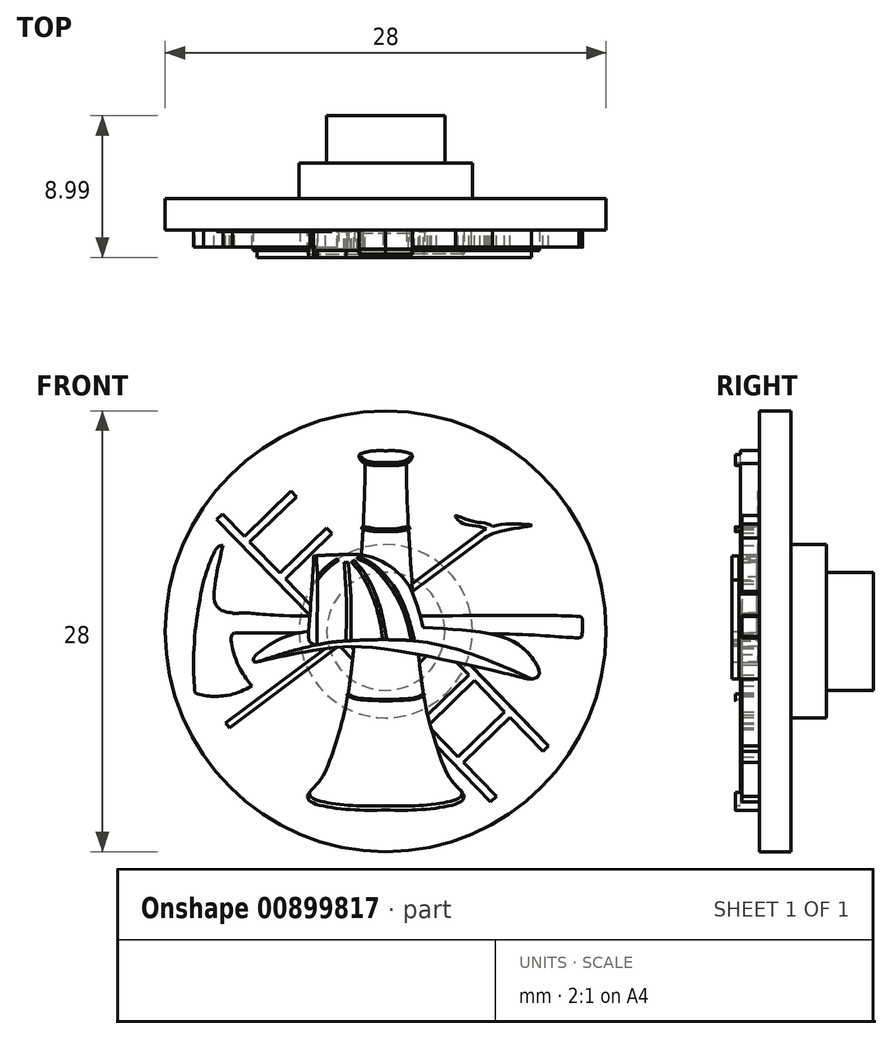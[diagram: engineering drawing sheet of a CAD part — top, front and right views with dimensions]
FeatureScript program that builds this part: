
annotation { "Feature Type Name" : "Feature", "Feature Type Description" : "" }
export const myFeature = defineFeature(function(context is Context, id is Id, definition is map)
    precondition{}
    {
        {
            var Q0;
            Q0=qCreatedBy(makeId("Top.planeOp"),FACE);
            var sketch = newSketch(context, id + "F0", { "sketchPlane" : qUnion([Q0])});
            skLineSegment(sketch, "E0", {"start": v(0, 0) * mm, "end": v(-14, 0) * mm});
            skLineSegment(sketch, "E1", {"start": v(-14, 0) * mm, "end": v(-14, 2) * mm});
            skLineSegment(sketch, "E2", {"start": v(-14, 2) * mm, "end": v(-5.5, 2) * mm});
            skLineSegment(sketch, "E3", {"start": v(-5.5, 2) * mm, "end": v(-5.5, 4.25) * mm});
            skLineSegment(sketch, "E4", {"start": v(-5.5, 4.25) * mm, "end": v(-3.75, 4.25) * mm});
            skLineSegment(sketch, "E5", {"start": v(-3.75, 4.25) * mm, "end": v(-3.75, 7.25) * mm});
            skLineSegment(sketch, "E6", {"start": v(-3.75, 7.25) * mm, "end": v(0, 7.25) * mm});
            skLineSegment(sketch, "E7", {"start": v(0, 7.25) * mm, "end": v(0, 0) * mm});
            skSolve(sketch);
        }
        {
            var Q0;
            Q0=makeQuery(id+"F0.imprint","IMPRINT",FACE,{"disambiguationData":[TD([[makeQuery(id+"F0.imprint","IMPRINT",EDGE,{"derivedFrom":sQuery(id+"F0.wireOp",EDGE,"E0")}),-1.0]])]});
            var Q1;
            Q1=sQuery(id+"F0.wireOp",EDGE,"E7");
            revolve(context, id + "F1", {"surfaceOperationType" : NewSurfaceOperationType.NEW, "entities" : qUnion([Q0]), "axis" : qUnion([Q1]), "revolveType" : RevolveType.FULL});
        }
        {
            var Q0;
            Q0=makeQuery(id+"F1.opRevolve","SWEPT_FACE",FACE,{"disambiguationData":[OSD([sQuery(id+"F0.wireOp",EDGE,"E0")])]});
            var sketch = newSketch(context, id + "F2", { "sketchPlane" : qUnion([Q0])});
            skFitSpline(sketch, "E8", {"points": [v(-4.9, 0) * mm, v(-6.87, -0.58) * mm, v(-8.37, -1.68) * mm, v(-8.37, -1.91) * mm, v(-8.17, -1.94) * mm, v(-7.37, -1.76) * mm, v(-4.83, -1.26) * mm, v(-0.5, -1.08) * mm, v(8.76, -2.96) * mm, v(9.26, -3.03) * mm, v(9.64, -2.89) * mm, v(9.74, -2.52) * mm, v(8.83, -1.16) * mm, v(7, -0.24) * mm, v(2.37, 0.26) * mm], "startDerivative": vector(-35.31, -5.38) * mm, "endDerivative": vector(-43.26, 2.75) * mm});
            skFitSpline(sketch, "E9", {"points": [v(-8.17, -1.94) * mm, v(-5.98, -1.26) * mm, v(-3.2, -0.69) * mm, v(0.5, -0.54) * mm, v(2.72, -0.73) * mm, v(5.57, -1.5) * mm, v(9.26, -3.03) * mm], "startDerivative": vector(14.7, 4.83) * mm, "endDerivative": vector(19.38, -8.65) * mm});
            skFitSpline(sketch, "E10", {"points": [v(2.37, 0.26) * mm, v(1.88, 1.97) * mm, v(1, 3.5) * mm, v(-0.83, 4.69) * mm, v(-2.82, 4.87) * mm, v(-4.57, 4.77) * mm, v(-4.58, 4.74) * mm, v(-4.9, 0) * mm], "startDerivative": vector(-2.96, 11.42) * mm, "endDerivative": vector(-2.12, -28.99) * mm});
            skFitSpline(sketch, "E11", {"points": [v(-4.9, 0) * mm, v(-4.9, -0.32) * mm, v(-4.9, -0.47) * mm, v(-4.84, -0.63) * mm, v(-4.71, -0.76) * mm, v(-4.56, -0.84) * mm, v(-4.38, -0.87) * mm], "startDerivative": vector(-0.09, -1.67) * mm, "endDerivative": vector(1.14, -0.23) * mm});
            skFitSpline(sketch, "E12", {"points": [v(-4.42, 4.8) * mm, v(-4.3, 2.68) * mm, v(-4.38, -0.87) * mm], "startDerivative": vector(0.36, -4.54) * mm, "endDerivative": vector(-0.25, -6.7) * mm});
            skFitSpline(sketch, "E13", {"points": [v(-3.3, 4.85) * mm, v(-2.95, 4.47) * mm, v(-2.16, 4.43) * mm, v(-1.61, 4.85) * mm], "startDerivative": vector(0.93, -1.49) * mm, "endDerivative": vector(1.38, 1.52) * mm});
            skFitSpline(sketch, "E14", {"points": [v(-3.1, 4.58) * mm, v(-3.57, 4.26) * mm, v(-4.33, 3.45) * mm], "startDerivative": vector(-1.19, -0.58) * mm, "endDerivative": vector(-1.01, -1.73) * mm});
            skFitSpline(sketch, "E15", {"points": [v(-4.32, 3.25) * mm, v(-3.5, 4.14) * mm, v(-3, 4.5) * mm], "startDerivative": vector(1.26, 1.99) * mm, "endDerivative": vector(1.19, 0.64) * mm});
            skFitSpline(sketch, "E16", {"points": [v(-2.65, 4.38) * mm, v(-2.5, 2.04) * mm, v(-2.52, -0.62) * mm], "startDerivative": vector(0.38, -4.75) * mm, "endDerivative": vector(-0.12, -5.26) * mm});
            skFitSpline(sketch, "E17", {"points": [v(-2.37, 4.38) * mm, v(-2.2, 2.04) * mm, v(-2.22, -0.6) * mm], "startDerivative": vector(0.43, -4.74) * mm, "endDerivative": vector(-0.12, -5.23) * mm});
            skFitSpline(sketch, "E18", {"points": [v(-2.18, 4.42) * mm, v(-1.46, 3.46) * mm, v(-0.77, 2.02) * mm, v(-0.43, 0.87) * mm, v(-0.19, -0.53) * mm], "startDerivative": vector(3.15, -3.72) * mm, "endDerivative": vector(0.9, -5.7) * mm});
            skFitSpline(sketch, "E19", {"points": [v(-2, 4.5) * mm, v(-1.28, 3.62) * mm, v(-0.56, 2.13) * mm, v(-0.21, 0.93) * mm, v(0.06, -0.53) * mm], "startDerivative": vector(3.23, -3.46) * mm, "endDerivative": vector(1, -5.88) * mm});
            skFitSpline(sketch, "E20", {"points": [v(-1.83, 4.63) * mm, v(-0.84, 4.1) * mm, v(0.22, 2.9) * mm, v(1.07, 1.4) * mm, v(1.62, -0.59) * mm], "startDerivative": vector(4.78, -2.05) * mm, "endDerivative": vector(1.66, -7.34) * mm});
            skFitSpline(sketch, "E21", {"points": [v(-1.73, 4.73) * mm, v(-0.8, 4.28) * mm, v(0.38, 3.04) * mm, v(1.23, 1.48) * mm, v(1.83, -0.6) * mm], "startDerivative": vector(4.6, -1.74) * mm, "endDerivative": vector(1.86, -7.6) * mm});
            skSolve(sketch);
        }
        {
            var Q0;
            Q0=makeQuery(id+"F1.opRevolve","SWEPT_FACE",FACE,{"disambiguationData":[OSD([sQuery(id+"F0.wireOp",EDGE,"E0")])]});
            var sketch = newSketch(context, id + "F3", { "sketchPlane" : qUnion([Q0])});
            skFitSpline(sketch, "E22", {"points": [v(-1.3, 10.65) * mm, v(-1.42, 6.93) * mm, v(-2.3, -3.39) * mm, v(-2.96, -6.4) * mm, v(-3.66, -8.52) * mm, v(-4.31, -9.64) * mm, v(-4.96, -10.4) * mm, v(-4.84, -10.76) * mm, v(-3.9, -11.11) * mm, v(-1.9, -11.35) * mm, v(0, -11.35) * mm], "startDerivative": vector(-0.32, -23.25) * mm, "endDerivative": vector(20.07, 0.5) * mm});
            skFitSpline(sketch, "E23", {"points": [v(-2.4, -3.98) * mm, v(-1.81, -4.23) * mm, v(-1.11, -4.3) * mm, v(-0.55, -4.33) * mm, v(0, -4.33) * mm], "startDerivative": vector(2.26, -1.15) * mm, "endDerivative": vector(2.35, 0.04) * mm});
            skFitSpline(sketch, "E24", {"points": [v(-2.4, -3.98) * mm, v(-2.45, -4) * mm, v(-2.41, -4.08) * mm, v(-1.83, -4.31) * mm, v(-1.1, -4.38) * mm, v(-0.55, -4.4) * mm, v(0, -4.41) * mm], "startDerivative": vector(-1, -0.29) * mm, "endDerivative": vector(2.72, -0.01) * mm});
            skFitSpline(sketch, "E25", {"points": [v(-4.86, -10.22) * mm, v(-4.72, -10.55) * mm, v(-3.84, -10.86) * mm, v(-1.97, -11.07) * mm, v(0, -11.1) * mm], "startDerivative": vector(0.49, -2.53) * mm, "endDerivative": vector(6.03, 0) * mm});
            skFitSpline(sketch, "E26", {"points": [v(0, 6.5) * mm, v(-0.7, 6.52) * mm, v(-1.44, 6.63) * mm, v(-1.52, 6.58) * mm, v(-1.51, 6.52) * mm, v(-0.74, 6.35) * mm, v(0, 6.34) * mm], "startDerivative": vector(-3.13, -0.1) * mm, "endDerivative": vector(3.11, 0.12) * mm});
            skFitSpline(sketch, "E27", {"points": [v(0, 11.46) * mm, v(-0.68, 11.46) * mm, v(-1.26, 11.38) * mm, v(-1.66, 11.21) * mm, v(-1.66, 10.98) * mm, v(-1.3, 10.65) * mm, v(0, 10.54) * mm], "startDerivative": vector(-3.85, 0.1) * mm, "endDerivative": vector(5.99, 0.16) * mm});
            skFitSpline(sketch, "E28", {"points": [v(0, 10.73) * mm, v(-1.23, 10.83) * mm, v(-1.66, 11.21) * mm], "startDerivative": vector(-2.37, -0.06) * mm, "endDerivative": vector(-0.85, 1.1) * mm});
            skFitSpline(sketch, "E29.MirrorCS", {"points": [v(0, 11.46) * mm, v(0.68, 11.46) * mm, v(1.26, 11.38) * mm, v(1.66, 11.21) * mm, v(1.66, 10.98) * mm, v(1.3, 10.65) * mm, v(0, 10.54) * mm], "startDerivative": vector(3.85, 0.1) * mm, "endDerivative": vector(-5.99, 0.16) * mm});
            skFitSpline(sketch, "E30.MirrorCS", {"points": [v(0, 10.73) * mm, v(1.23, 10.83) * mm, v(1.66, 11.21) * mm], "startDerivative": vector(2.37, -0.06) * mm, "endDerivative": vector(0.85, 1.1) * mm});
            skFitSpline(sketch, "E31.MirrorCS", {"points": [v(1.3, 10.65) * mm, v(1.42, 6.93) * mm, v(2.3, -3.39) * mm, v(2.96, -6.4) * mm, v(3.66, -8.52) * mm, v(4.31, -9.64) * mm, v(4.96, -10.4) * mm, v(4.84, -10.76) * mm, v(3.9, -11.11) * mm, v(1.9, -11.35) * mm, v(0, -11.35) * mm], "startDerivative": vector(0.32, -23.25) * mm, "endDerivative": vector(-20.07, 0.5) * mm});
            skFitSpline(sketch, "E32.MirrorCS", {"points": [v(0, 6.5) * mm, v(0.7, 6.52) * mm, v(1.44, 6.63) * mm, v(1.52, 6.58) * mm, v(1.51, 6.52) * mm, v(0.74, 6.35) * mm, v(0, 6.34) * mm], "startDerivative": vector(3.13, -0.1) * mm, "endDerivative": vector(-3.11, 0.12) * mm});
            skFitSpline(sketch, "E33.MirrorCS", {"points": [v(4.86, -10.22) * mm, v(4.72, -10.55) * mm, v(3.84, -10.86) * mm, v(1.97, -11.07) * mm, v(0, -11.1) * mm], "startDerivative": vector(-0.49, -2.53) * mm, "endDerivative": vector(-6.03, 0) * mm});
            skFitSpline(sketch, "E34.MirrorCS", {"points": [v(2.4, -3.98) * mm, v(1.81, -4.23) * mm, v(1.11, -4.3) * mm, v(0.55, -4.33) * mm, v(0, -4.33) * mm], "startDerivative": vector(-2.26, -1.15) * mm, "endDerivative": vector(-2.35, 0.04) * mm});
            skFitSpline(sketch, "E35.MirrorCS", {"points": [v(2.4, -3.98) * mm, v(2.45, -4) * mm, v(2.41, -4.08) * mm, v(1.83, -4.31) * mm, v(1.1, -4.38) * mm, v(0.55, -4.4) * mm, v(0, -4.41) * mm], "startDerivative": vector(1, -0.29) * mm, "endDerivative": vector(-2.72, -0.01) * mm});
            skSolve(sketch);
        }
        {
            var Q0;
            Q0=makeQuery(id+"F2.imprint","IMPRINT",FACE,{"disambiguationData":[TD([[makeQuery(id+"F2.imprint","IMPRINT",EDGE,{"derivedFrom":makeQuery(id+"F1.opRevolve","SWEPT_EDGE",EDGE,{"disambiguationData":[OSD([sQuery(id+"F0.wireOp",EDGE,"E0"),sQuery(id+"F0.wireOp",EDGE,"E1")])]})}),-1.0]])]});
            var sketch = newSketch(context, id + "F4", { "sketchPlane" : qUnion([Q0])});
            skLineSegment(sketch, "E36", {"start": v(7.02, -10.5) * mm, "end": v(-10.37, 7.46) * mm});
            skLineSegment(sketch, "E37", {"start": v(-10.37, 7.46) * mm, "end": v(-10.73, 7.11) * mm});
            skLineSegment(sketch, "E38", {"start": v(-10.73, 7.11) * mm, "end": v(6.66, -10.84) * mm});
            skLineSegment(sketch, "E39", {"start": v(6.66, -10.84) * mm, "end": v(7.02, -10.5) * mm});
            skLineSegment(sketch, "E40", {"start": v(-10.73, 7.11) * mm, "end": v(-6.65, 11.07) * mm, "construction": true});
            skLineSegment(sketch, "E41", {"start": v(6.66, -10.84) * mm, "end": v(10.92, -6.71) * mm, "construction": true});
            skLineSegment(sketch, "E42", {"start": v(-7.41, 10.33) * mm, "end": v(9.99, -7.62) * mm});
            skLineSegment(sketch, "E43", {"start": v(9.99, -7.62) * mm, "end": v(10.35, -7.27) * mm});
            skLineSegment(sketch, "E44", {"start": v(10.35, -7.27) * mm, "end": v(-7.05, 10.68) * mm});
            skLineSegment(sketch, "E45", {"start": v(-8.98, 6.02) * mm, "end": v(-6.02, 8.9) * mm});
            skLineSegment(sketch, "E46", {"start": v(-6.02, 8.9) * mm, "end": v(-5.67, 8.54) * mm});
            skLineSegment(sketch, "E47", {"start": v(-5.67, 8.54) * mm, "end": v(-8.63, 5.67) * mm});
            skLineSegment(sketch, "E48", {"start": v(-6.72, 3.7) * mm, "end": v(-3.76, 6.56) * mm});
            skLineSegment(sketch, "E49", {"start": v(-3.4, 6.2) * mm, "end": v(-6.37, 3.33) * mm});
            skLineSegment(sketch, "E50", {"start": v(-4.46, 1.36) * mm, "end": v(-1.5, 4.23) * mm});
            skLineSegment(sketch, "E51", {"start": v(-1.15, 3.87) * mm, "end": v(-4.11, 1) * mm});
            skLineSegment(sketch, "E52", {"start": v(-2.2, -0.98) * mm, "end": v(0.77, 1.9) * mm});
            skLineSegment(sketch, "E53", {"start": v(1.11, 1.53) * mm, "end": v(-1.85, -1.34) * mm});
            skLineSegment(sketch, "E54", {"start": v(3.03, -0.44) * mm, "end": v(0.06, -3.31) * mm});
            skLineSegment(sketch, "E55", {"start": v(0.41, -3.67) * mm, "end": v(3.38, -0.8) * mm});
            skLineSegment(sketch, "E56", {"start": v(5.29, -2.77) * mm, "end": v(2.33, -5.65) * mm});
            skLineSegment(sketch, "E57", {"start": v(2.33, -5.65) * mm, "end": v(2.67, -6) * mm});
            skLineSegment(sketch, "E58", {"start": v(2.67, -6) * mm, "end": v(5.64, -3.13) * mm});
            skLineSegment(sketch, "E59", {"start": v(7.55, -5.1) * mm, "end": v(4.59, -7.98) * mm});
            skLineSegment(sketch, "E60", {"start": v(4.59, -7.98) * mm, "end": v(4.94, -8.34) * mm});
            skLineSegment(sketch, "E61", {"start": v(4.94, -8.34) * mm, "end": v(7.9, -5.47) * mm});
            skLineSegment(sketch, "E62", {"start": v(-7.41, 10.33) * mm, "end": v(-7.05, 10.68) * mm});
            skSolve(sketch);
        }
        {
            var Q0;
            Q0=makeQuery(id+"F2.imprint","IMPRINT",FACE,{"disambiguationData":[TD([[makeQuery(id+"F2.imprint","IMPRINT",EDGE,{"derivedFrom":makeQuery(id+"F1.opRevolve","SWEPT_EDGE",EDGE,{"disambiguationData":[OSD([sQuery(id+"F0.wireOp",EDGE,"E0"),sQuery(id+"F0.wireOp",EDGE,"E1")])]})}),-1.0]])]});
            var sketch = newSketch(context, id + "F5", { "sketchPlane" : qUnion([Q0])});
            skLineSegment(sketch, "E63", {"start": v(-10.17, -5.8) * mm, "end": v(6, 6.23) * mm});
            skLineSegment(sketch, "E64", {"start": v(-10.17, -5.8) * mm, "end": v(-9.93, -6.13) * mm});
            skLineSegment(sketch, "E65", {"start": v(-9.93, -6.13) * mm, "end": v(6.28, 5.94) * mm});
            skFitSpline(sketch, "E66", {"points": [v(6, 6.23) * mm, v(7.48, 6.8) * mm, v(9.26, 6.72) * mm, v(7.7, 6.45) * mm, v(6.28, 5.94) * mm], "startDerivative": vector(3.7, 3.49) * mm, "endDerivative": vector(-4.19, -2.44) * mm});
            skFitSpline(sketch, "E67", {"points": [v(6.78, 6.66) * mm, v(6.3, 6.87) * mm, v(5.36, 7.03) * mm, v(4.42, 7.34) * mm, v(4.7, 6.96) * mm, v(5.29, 6.75) * mm, v(6.08, 6.62) * mm, v(6.38, 6.5) * mm], "startDerivative": vector(-2.93, 2.6) * mm, "endDerivative": vector(2.44, -1.25) * mm});
            skSolve(sketch);
        }
        {
            var Q0;
            Q0=makeQuery(id+"F2.imprint","IMPRINT",FACE,{"disambiguationData":[TD([[makeQuery(id+"F2.imprint","IMPRINT",EDGE,{"derivedFrom":makeQuery(id+"F1.opRevolve","SWEPT_EDGE",EDGE,{"disambiguationData":[OSD([sQuery(id+"F0.wireOp",EDGE,"E0"),sQuery(id+"F0.wireOp",EDGE,"E1")])]})}),-1.0]])]});
            var sketch = newSketch(context, id + "F6", { "sketchPlane" : qUnion([Q0])});
            skFitSpline(sketch, "E68", {"points": [v(-11.56, 3.2) * mm, v(-12, 0.78) * mm, v(-12.2, -2.34) * mm, v(-12.1, -3.93) * mm], "startDerivative": vector(-1.44, -6.68) * mm, "endDerivative": vector(0.51, -5.2) * mm});
            skFitSpline(sketch, "E69", {"points": [v(-12.1, -3.93) * mm, v(-11.33, -4.11) * mm, v(-10.57, -4.13) * mm, v(-9.66, -3.98) * mm, v(-8.5, -3.48) * mm], "startDerivative": vector(3.35, -0.94) * mm, "endDerivative": vector(4.06, 1.98) * mm});
            skFitSpline(sketch, "E70", {"points": [v(-8.5, -3.48) * mm, v(-9.36, -2.17) * mm, v(-9.8, -0.28) * mm, v(-9.59, -0.12) * mm], "startDerivative": vector(-2.28, 2.73) * mm, "endDerivative": vector(1.56, 0.49) * mm});
            skFitSpline(sketch, "E71", {"points": [v(-9.59, -0.12) * mm, v(-9.7, 0) * mm, v(-9.72, 1.16) * mm], "startDerivative": vector(-0.42, 0.28) * mm, "endDerivative": vector(0.09, 2) * mm});
            skFitSpline(sketch, "E72", {"points": [v(-9.72, 1.16) * mm, v(-10.32, 1.3) * mm, v(-10.78, 1.66) * mm, v(-10.88, 2.7) * mm, v(-10.34, 5.46) * mm], "startDerivative": vector(-3.36, 0.47) * mm, "endDerivative": vector(1.77, 7.66) * mm});
            skFitSpline(sketch, "E73", {"points": [v(-10.34, 5.46) * mm, v(-10.7, 5.31) * mm, v(-11.56, 3.2) * mm], "startDerivative": vector(-1.2, -0.16) * mm, "endDerivative": vector(-1.24, -3.83) * mm});
            skFitSpline(sketch, "E74", {"points": [v(-9.72, 1.11) * mm, v(-8.95, 1.16) * mm, v(-6.69, 1) * mm, v(8.74, 1.02) * mm, v(12.28, 0.94) * mm], "startDerivative": vector(7, 0.73) * mm, "endDerivative": vector(11.01, -0.48) * mm});
            skFitSpline(sketch, "E75", {"points": [v(12.28, 0.94) * mm, v(12.44, 0.88) * mm, v(12.46, -0.34) * mm], "startDerivative": vector(0.67, -0.04) * mm, "endDerivative": vector(-0.18, -2.2) * mm});
            skFitSpline(sketch, "E76", {"points": [v(12.46, -0.34) * mm, v(12.36, -0.4) * mm, v(9.57, -0.26) * mm, v(-9.59, -0.12) * mm], "startDerivative": vector(-1.31, -1.2) * mm, "endDerivative": vector(-33.19, -0.18) * mm});
            skSolve(sketch);
        }
        {
            var Q0;
            Q0=makeQuery(id+"F6.imprint","IMPRINT",FACE,{"disambiguationData":[TD([[makeQuery(id+"F6.imprint","IMPRINT",EDGE,{"derivedFrom":sQuery(id+"F6.wireOp",EDGE,"E68")}),1.0]])]});
            var Q1;
            {var subQ0=sQuery(id+"F6.wireOp",EDGE,"E74");var subQ1=sQuery(id+"F6.wireOp",EDGE,"E71");var subQ2=makeQuery(id+"F6.imprint","INTERSECT",VERTEX,{"derivedFrom":[subQ1,subQ0]});Q1=makeQuery(id+"F6.imprint","IMPRINT",FACE,{"disambiguationData":[TD([[makeQuery(id+"F6.imprint","IMPRINT",EDGE,{"disambiguationData":[TD([[subQ2,1.0]])],"derivedFrom":subQ1}),-1.0]])]});}
            var Q2;
            {var subQ1=sQuery(id+"F6.wireOp",EDGE,"E75");Q2=makeQuery(id+"F6.imprint","IMPRINT",FACE,{"disambiguationData":[TD([[makeQuery(id+"F6.imprint","IMPRINT",EDGE,{"derivedFrom":subQ1}),-1.0]])]});}
            extrude(context, id + "F7", {"entities" : qUnion([Q0, Q1, Q2]), "operationType" : NewBodyOperationType.ADD, "depth" : .1 * mm, "offsetDistance" : 25 * mm});
        }
        {
            var Q0;
            {var subQ0=sQuery(id+"F5.wireOp",EDGE,"E64");Q0=makeQuery(id+"F5.imprint","IMPRINT",FACE,{"disambiguationData":[TD([[makeQuery(id+"F5.imprint","IMPRINT",EDGE,{"derivedFrom":subQ0}),1.0]])]});}
            var Q1;
            {var subQ1=sQuery(id+"F5.wireOp",EDGE,"E66");var subQ9=sQuery(id+"F5.wireOp",EDGE,"E63");var subQ10=makeQuery(id+"F5.imprint","INTERSECT",VERTEX,{"derivedFrom":[subQ9,subQ1]});Q1=makeQuery(id+"F5.imprint","IMPRINT",FACE,{"disambiguationData":[TD([[makeQuery(id+"F5.imprint","IMPRINT",EDGE,{"disambiguationData":[TD([[subQ10,-1.0]])],"derivedFrom":subQ1}),-1.0]])]});}
            var Q2;
            {var subQ0=sQuery(id+"F5.wireOp",EDGE,"E67");Q2=makeQuery(id+"F5.imprint","IMPRINT",FACE,{"disambiguationData":[TD([[makeQuery(id+"F5.imprint","IMPRINT",EDGE,{"derivedFrom":subQ0}),1.0]])]});}
            extrude(context, id + "F8", {"entities" : qUnion([Q0, Q1, Q2]), "operationType" : NewBodyOperationType.ADD, "depth" : .1 * mm, "offsetDistance" : 25 * mm});
        }
        {
            var Q0;
            {var subQ10=sQuery(id+"F4.wireOp",EDGE,"E37");Q0=makeQuery(id+"F4.imprint","IMPRINT",FACE,{"disambiguationData":[TD([[makeQuery(id+"F4.imprint","IMPRINT",EDGE,{"derivedFrom":subQ10}),1.0]])]});}
            var Q1;
            {var subQ0=sQuery(id+"F4.wireOp",EDGE,"E45");Q1=makeQuery(id+"F4.imprint","IMPRINT",FACE,{"disambiguationData":[TD([[makeQuery(id+"F4.imprint","IMPRINT",EDGE,{"derivedFrom":subQ0}),-1.0]])]});}
            var Q2;
            {var subQ0=sQuery(id+"F4.wireOp",EDGE,"E48");Q2=makeQuery(id+"F4.imprint","IMPRINT",FACE,{"disambiguationData":[TD([[makeQuery(id+"F4.imprint","IMPRINT",EDGE,{"derivedFrom":subQ0}),-1.0]])]});}
            var Q3;
            {var subQ8=sQuery(id+"F4.wireOp",EDGE,"E46");Q3=makeQuery(id+"F4.imprint","IMPRINT",FACE,{"disambiguationData":[TD([[makeQuery(id+"F4.imprint","IMPRINT",EDGE,{"derivedFrom":subQ8}),1.0]])]});}
            var Q4;
            {var subQ0=sQuery(id+"F4.wireOp",EDGE,"E39");Q4=makeQuery(id+"F4.imprint","IMPRINT",FACE,{"disambiguationData":[TD([[makeQuery(id+"F4.imprint","IMPRINT",EDGE,{"derivedFrom":subQ0}),1.0]])]});}
            var Q5;
            {var subQ0=sQuery(id+"F4.wireOp",EDGE,"E56");Q5=makeQuery(id+"F4.imprint","IMPRINT",FACE,{"disambiguationData":[TD([[makeQuery(id+"F4.imprint","IMPRINT",EDGE,{"derivedFrom":subQ0}),1.0]])]});}
            var Q6;
            {var subQ0=sQuery(id+"F4.wireOp",EDGE,"E59");Q6=makeQuery(id+"F4.imprint","IMPRINT",FACE,{"disambiguationData":[TD([[makeQuery(id+"F4.imprint","IMPRINT",EDGE,{"derivedFrom":subQ0}),1.0]])]});}
            extrude(context, id + "F9", {"entities" : qUnion([Q0, Q1, Q2, Q3, Q4, Q5, Q6]), "operationType" : NewBodyOperationType.ADD, "depth" : .1 * mm, "offsetDistance" : 25 * mm});
        }
        {
            var Q0;
            {var subQ9=sQuery(id+"F4.wireOp",EDGE,"E43");Q0=makeQuery(id+"F4.imprint","IMPRINT",FACE,{"disambiguationData":[TD([[makeQuery(id+"F4.imprint","IMPRINT",EDGE,{"derivedFrom":subQ9}),1.0]])]});}
            var Q1;
            {var subQ0=sQuery(id+"F4.wireOp",EDGE,"E42");var subQ20=makeQuery(id+"F4.imprint","INTERSECT",VERTEX,{"derivedFrom":[subQ0,sQuery(id+"F4.wireOp",EDGE,"E50")]});Q1=makeQuery(id+"F4.imprint","IMPRINT",FACE,{"disambiguationData":[TD([[makeQuery(id+"F4.imprint","IMPRINT",EDGE,{"disambiguationData":[TD([[subQ20,-1.0]])],"derivedFrom":subQ0}),1.0]])]});}
            extrude(context, id + "F10", {"entities" : qUnion([Q0, Q1]), "operationType" : NewBodyOperationType.ADD, "depth" : .1 * mm, "offsetDistance" : 25 * mm});
        }
        {
            var Q0;
            {var subQ0=sQuery(id+"F4.wireOp",EDGE,"E54");var subQ1=sQuery(id+"F4.wireOp",EDGE,"E36");var subQ2=makeQuery(id+"F4.imprint","INTERSECT",VERTEX,{"derivedFrom":[subQ1,subQ0]});Q0=makeQuery(id+"F4.imprint","IMPRINT",FACE,{"disambiguationData":[TD([[makeQuery(id+"F4.imprint","IMPRINT",EDGE,{"disambiguationData":[TD([[subQ2,1.0]])],"derivedFrom":subQ1}),-1.0]])]});}
            extrude(context, id + "F11", {"entities" : qUnion([Q0]), "operationType" : NewBodyOperationType.ADD, "depth" : .1 * mm, "offsetDistance" : 25 * mm});
        }
        {
            var Q0;
            {var subQ8=sQuery(id+"F3.wireOp",EDGE,"E23");Q0=makeQuery(id+"F3.imprint","IMPRINT",FACE,{"disambiguationData":[TD([[makeQuery(id+"F3.imprint","IMPRINT",EDGE,{"derivedFrom":subQ8}),1.0]])]});}
            var Q1;
            {var subQ8=sQuery(id+"F3.wireOp",EDGE,"E25");Q1=makeQuery(id+"F3.imprint","IMPRINT",FACE,{"disambiguationData":[TD([[makeQuery(id+"F3.imprint","IMPRINT",EDGE,{"derivedFrom":subQ8}),1.0]])]});}
            var Q2;
            {var subQ1=sQuery(id+"F3.wireOp",EDGE,"E27");var subQ5=sQuery(id+"F3.wireOp",EDGE,"E22");var subQ6=makeQuery(id+"F3.imprint","INTERSECT",VERTEX,{"derivedFrom":[subQ5,subQ1]});Q2=makeQuery(id+"F3.imprint","IMPRINT",FACE,{"disambiguationData":[TD([[makeQuery(id+"F3.imprint","IMPRINT",EDGE,{"disambiguationData":[TD([[subQ6,-1.0]])],"derivedFrom":subQ5}),1.0]])]});}
            var Q3;
            {var subQ3=sQuery(id+"F3.wireOp",EDGE,"E28");Q3=makeQuery(id+"F3.imprint","IMPRINT",FACE,{"disambiguationData":[TD([[makeQuery(id+"F3.imprint","IMPRINT",EDGE,{"derivedFrom":subQ3}),-1.0]])]});}
            extrude(context, id + "F12", {"entities" : qUnion([Q0, Q1, Q2, Q3]), "operationType" : NewBodyOperationType.ADD, "depth" : .2 * mm, "offsetDistance" : 25 * mm});
        }
        {
            var Q0;
            {var subQ3=sQuery(id+"F3.wireOp",EDGE,"E28");Q0=makeQuery(id+"F3.imprint","IMPRINT",FACE,{"disambiguationData":[TD([[makeQuery(id+"F3.imprint","IMPRINT",EDGE,{"derivedFrom":subQ3}),1.0]])]});}
            var Q1;
            {var subQ4=sQuery(id+"F3.wireOp",EDGE,"E26");var subQ6=sQuery(id+"F3.wireOp",EDGE,"E22");var subQ8=makeQuery(id+"F3.imprint","INTERSECT",VERTEX,{"disambiguationData":[OD(0.0)],"derivedFrom":[subQ6,subQ4]});Q1=makeQuery(id+"F3.imprint","IMPRINT",FACE,{"disambiguationData":[TD([[makeQuery(id+"F3.imprint","IMPRINT",EDGE,{"disambiguationData":[TD([[subQ8,-1.0]])],"derivedFrom":subQ6}),1.0]])]});}
            var Q2;
            {var subQ0=sQuery(id+"F3.wireOp",EDGE,"E32.MirrorCS");var subQ1=sQuery(id+"F3.wireOp",EDGE,"E31.MirrorCS");var subQ2=makeQuery(id+"F3.imprint","INTERSECT",VERTEX,{"disambiguationData":[OD(0.0)],"derivedFrom":[subQ1,subQ0]});Q2=makeQuery(id+"F3.imprint","IMPRINT",FACE,{"disambiguationData":[TD([[makeQuery(id+"F3.imprint","IMPRINT",EDGE,{"disambiguationData":[TD([[subQ2,-1.0]])],"derivedFrom":subQ1}),1.0]])]});}
            var Q3;
            {var subQ0=sQuery(id+"F3.wireOp",EDGE,"E26");var subQ1=sQuery(id+"F3.wireOp",EDGE,"E22");var subQ2=makeQuery(id+"F3.imprint","INTERSECT",VERTEX,{"disambiguationData":[OD(0.0)],"derivedFrom":[subQ1,subQ0]});Q3=makeQuery(id+"F3.imprint","IMPRINT",FACE,{"disambiguationData":[TD([[makeQuery(id+"F3.imprint","IMPRINT",EDGE,{"disambiguationData":[TD([[subQ2,-1.0]])],"derivedFrom":subQ1}),-1.0]])]});}
            var Q4;
            {var subQ4=sQuery(id+"F3.wireOp",EDGE,"E23");Q4=makeQuery(id+"F3.imprint","IMPRINT",FACE,{"disambiguationData":[TD([[makeQuery(id+"F3.imprint","IMPRINT",EDGE,{"derivedFrom":subQ4}),-1.0]])]});}
            var Q5;
            {var subQ0=sQuery(id+"F3.wireOp",EDGE,"E35.MirrorCS");var subQ1=sQuery(id+"F3.wireOp",EDGE,"E31.MirrorCS");var subQ3=makeQuery(id+"F3.imprint","INTERSECT",VERTEX,{"derivedFrom":[subQ1,subQ0]});Q5=makeQuery(id+"F3.imprint","IMPRINT",FACE,{"disambiguationData":[TD([[makeQuery(id+"F3.imprint","IMPRINT",EDGE,{"disambiguationData":[TD([[subQ3,1.0]])],"derivedFrom":subQ1}),1.0]])]});}
            var Q6;
            {var subQ0=sQuery(id+"F3.wireOp",EDGE,"E24");var subQ1=sQuery(id+"F3.wireOp",EDGE,"E22");var subQ3=makeQuery(id+"F3.imprint","INTERSECT",VERTEX,{"derivedFrom":[subQ1,subQ0]});Q6=makeQuery(id+"F3.imprint","IMPRINT",FACE,{"disambiguationData":[TD([[makeQuery(id+"F3.imprint","IMPRINT",EDGE,{"disambiguationData":[TD([[subQ3,1.0]])],"derivedFrom":subQ1}),-1.0]])]});}
            var Q7;
            {var subQ3=sQuery(id+"F3.wireOp",EDGE,"E25");Q7=makeQuery(id+"F3.imprint","IMPRINT",FACE,{"disambiguationData":[TD([[makeQuery(id+"F3.imprint","IMPRINT",EDGE,{"derivedFrom":subQ3}),-1.0]])]});}
            extrude(context, id + "F13", {"entities" : qUnion([Q0, Q1, Q2, Q3, Q4, Q5, Q6, Q7]), "operationType" : NewBodyOperationType.ADD, "depth" : .3 * mm, "offsetDistance" : 25 * mm});
        }
        {
            var Q0;
            {var subQ0=sQuery(id+"F2.wireOp",EDGE,"E9");var subQ4=sQuery(id+"F2.wireOp",EDGE,"E8");var subQ5=makeQuery(id+"F2.imprint","INTERSECT",VERTEX,{"disambiguationData":[OD(0.0)],"derivedFrom":[subQ4,subQ0]});Q0=makeQuery(id+"F2.imprint","IMPRINT",FACE,{"disambiguationData":[TD([[makeQuery(id+"F2.imprint","IMPRINT",EDGE,{"disambiguationData":[TD([[subQ5,-1.0]])],"derivedFrom":subQ4}),1.0]])]});}
            extrude(context, id + "F14", {"entities" : qUnion([Q0]), "operationType" : NewBodyOperationType.ADD, "depth" : .5 * mm, "offsetDistance" : 25 * mm});
        }
        {
            var Q0;
            {var subQ0=sQuery(id+"F2.wireOp",EDGE,"E11");Q0=makeQuery(id+"F2.imprint","IMPRINT",FACE,{"disambiguationData":[TD([[makeQuery(id+"F2.imprint","IMPRINT",EDGE,{"derivedFrom":subQ0}),-1.0]])]});}
            var Q1;
            {var subQ7=sQuery(id+"F2.wireOp",EDGE,"E21");Q1=makeQuery(id+"F2.imprint","IMPRINT",FACE,{"disambiguationData":[TD([[makeQuery(id+"F2.imprint","IMPRINT",EDGE,{"derivedFrom":subQ7}),1.0]])]});}
            extrude(context, id + "F15", {"entities" : qUnion([Q0, Q1]), "operationType" : NewBodyOperationType.ADD, "depth" : .3 * mm, "offsetDistance" : 25 * mm});
        }
        {
            var Q0;
            {var subQ5=sQuery(id+"F2.wireOp",EDGE,"E14");Q0=makeQuery(id+"F2.imprint","IMPRINT",FACE,{"disambiguationData":[TD([[makeQuery(id+"F2.imprint","IMPRINT",EDGE,{"derivedFrom":subQ5}),-1.0]])]});}
            var Q1;
            {var subQ0=sQuery(id+"F2.wireOp",EDGE,"E17");Q1=makeQuery(id+"F2.imprint","IMPRINT",FACE,{"disambiguationData":[TD([[makeQuery(id+"F2.imprint","IMPRINT",EDGE,{"derivedFrom":subQ0}),1.0]])]});}
            var Q2;
            {var subQ0=sQuery(id+"F2.wireOp",EDGE,"E15");Q2=makeQuery(id+"F2.imprint","IMPRINT",FACE,{"disambiguationData":[TD([[makeQuery(id+"F2.imprint","IMPRINT",EDGE,{"derivedFrom":subQ0}),-1.0]])]});}
            extrude(context, id + "F16", {"entities" : qUnion([Q0, Q1, Q2]), "operationType" : NewBodyOperationType.ADD, "depth" : .3 * mm, "offsetDistance" : 25 * mm});
        }
        {
            var Q0;
            {var subQ5=sQuery(id+"F2.wireOp",EDGE,"E11");Q0=makeQuery(id+"F2.imprint","IMPRINT",FACE,{"disambiguationData":[TD([[makeQuery(id+"F2.imprint","IMPRINT",EDGE,{"derivedFrom":subQ5}),1.0]])]});}
            var Q1;
            Q1=makeQuery(id+"F16.opExtrude","CAP_FACE",FACE,{"disambiguationData":[OSD([sQuery(id+"F2.wireOp",EDGE,"E9"),sQuery(id+"F2.wireOp",EDGE,"E12"),sQuery(id+"F2.wireOp",EDGE,"E13"),sQuery(id+"F2.wireOp",EDGE,"E15"),sQuery(id+"F2.wireOp",EDGE,"E16")])],"isStart":false});
            extrude(context, id + "F17", {"entities" : qUnion([Q0, Q1]), "operationType" : NewBodyOperationType.ADD, "depth" : .4 * mm, "offsetDistance" : 25 * mm});
        }
        {
            var Q0;
            {var subQ0=sQuery(id+"F2.wireOp",EDGE,"E19");Q0=makeQuery(id+"F2.imprint","IMPRINT",FACE,{"disambiguationData":[TD([[makeQuery(id+"F2.imprint","IMPRINT",EDGE,{"derivedFrom":subQ0}),1.0]])]});}
            var Q1;
            {var subQ0=sQuery(id+"F2.wireOp",EDGE,"E13");var subQ4=sQuery(id+"F2.wireOp",EDGE,"E10");var subQ5=makeQuery(id+"F2.imprint","INTERSECT",VERTEX,{"disambiguationData":[OD(0.0)],"derivedFrom":[subQ4,subQ0]});Q1=makeQuery(id+"F2.imprint","IMPRINT",FACE,{"disambiguationData":[TD([[makeQuery(id+"F2.imprint","IMPRINT",EDGE,{"disambiguationData":[TD([[subQ5,1.0]])],"derivedFrom":subQ4}),1.0]])]});}
            extrude(context, id + "F18", {"entities" : qUnion([Q0, Q1]), "operationType" : NewBodyOperationType.ADD, "depth" : .3 * mm, "offsetDistance" : 25 * mm});
        }
        {
            var Q0;
            Q0=makeQuery(id+"F17.opExtrude","CAP_FACE",FACE,{"disambiguationData":[OSD([sQuery(id+"F2.wireOp",EDGE,"E10"),sQuery(id+"F2.wireOp",EDGE,"E11"),sQuery(id+"F2.wireOp",EDGE,"E12")])],"isStart":false});
            extrude(context, id + "F19", {"entities" : qUnion([Q0]), "operationType" : NewBodyOperationType.ADD, "depth" : .1 * mm, "offsetDistance" : 25 * mm});
        }
        {
            var Q0;
            Q0=makeQuery(id+"F17.opExtrude","CAP_FACE",FACE,{"disambiguationData":[OSD([sQuery(id+"F2.wireOp",EDGE,"E9"),sQuery(id+"F2.wireOp",EDGE,"E12"),sQuery(id+"F2.wireOp",EDGE,"E13"),sQuery(id+"F2.wireOp",EDGE,"E15"),sQuery(id+"F2.wireOp",EDGE,"E16")])],"isStart":false});
            extrude(context, id + "F20", {"entities" : qUnion([Q0]), "operationType" : NewBodyOperationType.ADD, "depth" : 2 * mm, "offsetDistance" : 25 * mm});
        }
        {
            var Q0;
            Q0=makeQuery(id+"F20.opExtrude","CAP_FACE",FACE,{"disambiguationData":[OSD([sQuery(id+"F2.wireOp",EDGE,"E9"),sQuery(id+"F2.wireOp",EDGE,"E12"),sQuery(id+"F2.wireOp",EDGE,"E13"),sQuery(id+"F2.wireOp",EDGE,"E15"),sQuery(id+"F2.wireOp",EDGE,"E16")])],"isStart":false});
            extrude(context, id + "F21", {"entities" : qUnion([Q0]), "operationType" : NewBodyOperationType.REMOVE, "oppositeDirection" : true, "depth" : 2.2 * mm, "offsetDistance" : 25 * mm});
        }
        {
            var Q0;
            {var subQ0=sQuery(id+"F2.wireOp",EDGE,"E12");var subQ1=sQuery(id+"F2.wireOp",EDGE,"E9");Q0=makeQuery(id+"F21.boolean.opBoolean","MERGE",FACE,{"derivedFrom":[makeQuery(id+"F14.opExtrude","CAP_FACE",FACE,{"disambiguationData":[OSD([sQuery(id+"F2.wireOp",EDGE,"E8"),subQ1])],"isStart":false}),makeQuery(id+"F19.opExtrude","CAP_FACE",FACE,{"disambiguationData":[OSD([sQuery(id+"F2.wireOp",EDGE,"E10"),sQuery(id+"F2.wireOp",EDGE,"E11"),subQ0])],"isStart":false})],"fromTools":[makeQuery(id+"F21.opExtrude","CAP_FACE",FACE,{"disambiguationData":[OSD([subQ1,subQ0,sQuery(id+"F2.wireOp",EDGE,"E13"),sQuery(id+"F2.wireOp",EDGE,"E15"),sQuery(id+"F2.wireOp",EDGE,"E16")])],"isStart":false})]});}
            var sketch = newSketch(context, id + "F22", { "sketchPlane" : qUnion([Q0])});
            skLineSegment(sketch, "E77", {"start": v(-4.32, 3.25) * mm, "end": v(-4.38, -0.87) * mm});
            skFitSpline(sketch, "E78", {"points": [v(-4.38, -0.87) * mm, v(-3.46, -0.7) * mm, v(-2.52, -0.62) * mm], "startDerivative": vector(1.84, 0.4) * mm, "endDerivative": vector(1.87, 0.1) * mm});
            skLineSegment(sketch, "E79", {"start": v(-4.38, -0.81) * mm, "end": v(-4.35, -0.86) * mm});
            skSolve(sketch);
        }
        {
            var Q0;
            {var subQ9=sQuery(id+"F22.wireOp",EDGE,"E79");Q0=makeQuery(id+"F22.imprint","IMPRINT",FACE,{"disambiguationData":[TD([[makeQuery(id+"F22.imprint","IMPRINT",EDGE,{"derivedFrom":subQ9}),1.0]])]});}
            extrude(context, id + "F23", {"entities" : qUnion([Q0]), "operationType" : NewBodyOperationType.REMOVE, "oppositeDirection" : true, "depth" : .2 * mm, "offsetDistance" : 25 * mm});
        }
        {
            var Q0;
            Q0=makeQuery(id+"F7.opExtrude","CAP_FACE",FACE,{"disambiguationData":[OSD([sQuery(id+"F2.wireOp",EDGE,"E8"),sQuery(id+"F2.wireOp",EDGE,"E10"),sQuery(id+"F6.wireOp",EDGE,"E68"),sQuery(id+"F6.wireOp",EDGE,"E69"),sQuery(id+"F6.wireOp",EDGE,"E70"),sQuery(id+"F6.wireOp",EDGE,"E71"),sQuery(id+"F6.wireOp",EDGE,"E72"),sQuery(id+"F6.wireOp",EDGE,"E73"),sQuery(id+"F6.wireOp",EDGE,"E74"),sQuery(id+"F6.wireOp",EDGE,"E76")])],"isStart":false});
            var Q1;
            {var subQ0=sQuery(id+"F4.wireOp",EDGE,"E44");var subQ1=sQuery(id+"F2.wireOp",EDGE,"E10");var subQ2=sQuery(id+"F2.wireOp",EDGE,"E8");var subQ9=sQuery(id+"F6.wireOp",EDGE,"E76");var subQ10=sQuery(id+"F6.wireOp",EDGE,"E75");var subQ18=sQuery(id+"F4.wireOp",EDGE,"E43");var subQ20=makeQuery(id+"F7.opExtrude","SWEPT_FACE",FACE,{"disambiguationData":[OSD([subQ10])]});var subQ21=sQuery(id+"F4.wireOp",EDGE,"E49");var subQ22=sQuery(id+"F4.wireOp",EDGE,"E42");var subQ25=sQuery(id+"F6.wireOp",EDGE,"E74");var subQ33=sQuery(id+"F4.wireOp",EDGE,"E39");var subQ34=sQuery(id+"F4.wireOp",EDGE,"E38");var subQ35=sQuery(id+"F4.wireOp",EDGE,"E58");var subQ36=sQuery(id+"F4.wireOp",EDGE,"E36");var subQ38=sQuery(id+"F4.wireOp",EDGE,"E59");var subQ39=sQuery(id+"F4.wireOp",EDGE,"E61");var subQ40=sQuery(id+"F4.wireOp",EDGE,"E56");Q1=makeQuery(id+"F14.boolean.opBoolean","SPLIT",FACE,{"disambiguationData":[TD([subQ20])],"derivedFrom":makeQuery(id+"F12.boolean.opBoolean","SPLIT",FACE,{"disambiguationData":[TD([subQ20])],"derivedFrom":makeQuery(id+"F11.boolean.opBoolean","MERGE",FACE,{"derivedFrom":[makeQuery(id+"F10.boolean.opBoolean","MERGE",FACE,{"derivedFrom":[makeQuery(id+"F7.opExtrude","CAP_FACE",FACE,{"disambiguationData":[OSD([subQ2,subQ1,subQ25,subQ10,subQ9])],"isStart":false}),makeQuery(id+"F9.opExtrude","CAP_FACE",FACE,{"disambiguationData":[OSD([subQ2,subQ36,subQ34,subQ33,subQ22,subQ40,subQ35,subQ38,subQ39])],"isStart":false}),makeQuery(id+"F9.opExtrude","CAP_FACE",FACE,{"disambiguationData":[OSD([subQ1,subQ36,sQuery(id+"F4.wireOp",EDGE,"E37"),subQ34,subQ22,subQ0,sQuery(id+"F4.wireOp",EDGE,"E45"),sQuery(id+"F4.wireOp",EDGE,"E47"),sQuery(id+"F4.wireOp",EDGE,"E48"),subQ21,sQuery(id+"F4.wireOp",EDGE,"E62")])],"isStart":false}),makeQuery(id+"F10.opExtrude","CAP_FACE",FACE,{"disambiguationData":[OSD([subQ2,subQ1,subQ22,subQ18,subQ0])],"isStart":false})]}),makeQuery(id+"F11.opExtrude","CAP_FACE",FACE,{"disambiguationData":[OSD([subQ2,subQ36,sQuery(id+"F4.wireOp",EDGE,"E54"),sQuery(id+"F4.wireOp",EDGE,"E55")])],"isStart":false})]})})});}
            extrude(context, id + "F24", {"entities" : qUnion([Q0, Q1]), "operationType" : NewBodyOperationType.ADD, "depth" : 1 * mm, "offsetDistance" : 25 * mm});
        }
        {
            var Q0;
            {var subQ0=sQuery(id+"F4.wireOp",EDGE,"E42");var subQ2=sQuery(id+"F4.wireOp",EDGE,"E59");var subQ4=sQuery(id+"F4.wireOp",EDGE,"E58");var subQ5=sQuery(id+"F4.wireOp",EDGE,"E36");var subQ8=sQuery(id+"F4.wireOp",EDGE,"E61");var subQ10=sQuery(id+"F4.wireOp",EDGE,"E49");var subQ12=sQuery(id+"F2.wireOp",EDGE,"E10");var subQ15=sQuery(id+"F4.wireOp",EDGE,"E39");var subQ18=sQuery(id+"F4.wireOp",EDGE,"E56");var subQ20=makeQuery(id+"F9.opExtrude","SWEPT_FACE",FACE,{"disambiguationData":[OSD([subQ15])]});var subQ21=sQuery(id+"F4.wireOp",EDGE,"E38");var subQ23=sQuery(id+"F2.wireOp",EDGE,"E8");var subQ27=sQuery(id+"F4.wireOp",EDGE,"E43");var subQ29=sQuery(id+"F4.wireOp",EDGE,"E44");var subQ38=sQuery(id+"F6.wireOp",EDGE,"E76");var subQ40=sQuery(id+"F6.wireOp",EDGE,"E75");var subQ41=sQuery(id+"F6.wireOp",EDGE,"E74");Q0=makeQuery(id+"F14.boolean.opBoolean","SPLIT",FACE,{"disambiguationData":[TD([subQ20])],"derivedFrom":makeQuery(id+"F12.boolean.opBoolean","SPLIT",FACE,{"disambiguationData":[TD([makeQuery(id+"F7.opExtrude","SWEPT_FACE",FACE,{"disambiguationData":[OSD([subQ40])]})])],"derivedFrom":makeQuery(id+"F11.boolean.opBoolean","MERGE",FACE,{"derivedFrom":[makeQuery(id+"F10.boolean.opBoolean","MERGE",FACE,{"derivedFrom":[makeQuery(id+"F7.opExtrude","CAP_FACE",FACE,{"disambiguationData":[OSD([subQ23,subQ12,subQ41,subQ40,subQ38])],"isStart":false}),makeQuery(id+"F9.opExtrude","CAP_FACE",FACE,{"disambiguationData":[OSD([subQ23,subQ5,subQ21,subQ15,subQ0,subQ18,subQ4,subQ2,subQ8])],"isStart":false}),makeQuery(id+"F9.opExtrude","CAP_FACE",FACE,{"disambiguationData":[OSD([subQ12,subQ5,sQuery(id+"F4.wireOp",EDGE,"E37"),subQ21,subQ0,subQ29,sQuery(id+"F4.wireOp",EDGE,"E45"),sQuery(id+"F4.wireOp",EDGE,"E47"),sQuery(id+"F4.wireOp",EDGE,"E48"),subQ10,sQuery(id+"F4.wireOp",EDGE,"E62")])],"isStart":false}),makeQuery(id+"F10.opExtrude","CAP_FACE",FACE,{"disambiguationData":[OSD([subQ23,subQ12,subQ0,subQ27,subQ29])],"isStart":false})]}),makeQuery(id+"F11.opExtrude","CAP_FACE",FACE,{"disambiguationData":[OSD([subQ23,subQ5,sQuery(id+"F4.wireOp",EDGE,"E54"),sQuery(id+"F4.wireOp",EDGE,"E55")])],"isStart":false})]})})});}
            var sketch = newSketch(context, id + "F25", { "sketchPlane" : qUnion([Q0])});
            skLineSegment(sketch, "E80", {"start": v(4.52, -1.98) * mm, "end": v(5.4, -2.17) * mm});
            skSolve(sketch);
        }
        {
            var Q0;
            {var subQ23=sQuery(id+"F25.wireOp",EDGE,"E80");Q0=makeQuery(id+"F25.imprint","IMPRINT",FACE,{"disambiguationData":[TD([[makeQuery(id+"F25.imprint","IMPRINT",EDGE,{"derivedFrom":subQ23}),-1.0]])]});}
            var Q1;
            {var subQ0=sQuery(id+"F4.wireOp",EDGE,"E47");var subQ2=sQuery(id+"F4.wireOp",EDGE,"E42");var subQ3=sQuery(id+"F4.wireOp",EDGE,"E48");var subQ5=sQuery(id+"F4.wireOp",EDGE,"E62");var subQ6=sQuery(id+"F4.wireOp",EDGE,"E45");var subQ8=sQuery(id+"F4.wireOp",EDGE,"E38");var subQ9=sQuery(id+"F4.wireOp",EDGE,"E37");var subQ10=sQuery(id+"F2.wireOp",EDGE,"E10");var subQ11=sQuery(id+"F2.wireOp",EDGE,"E8");var subQ17=sQuery(id+"F4.wireOp",EDGE,"E49");var subQ21=sQuery(id+"F4.wireOp",EDGE,"E36");var subQ25=makeQuery(id+"F9.opExtrude","SWEPT_FACE",FACE,{"disambiguationData":[OSD([subQ9])]});var subQ26=sQuery(id+"F4.wireOp",EDGE,"E44");Q1=makeQuery(id+"F18.boolean.opBoolean","SPLIT",FACE,{"disambiguationData":[TD([subQ25])],"derivedFrom":makeQuery(id+"F12.boolean.opBoolean","SPLIT",FACE,{"disambiguationData":[TD([subQ25])],"derivedFrom":makeQuery(id+"F11.boolean.opBoolean","MERGE",FACE,{"derivedFrom":[makeQuery(id+"F10.boolean.opBoolean","MERGE",FACE,{"derivedFrom":[makeQuery(id+"F7.opExtrude","CAP_FACE",FACE,{"disambiguationData":[OSD([subQ11,subQ10,sQuery(id+"F6.wireOp",EDGE,"E74"),sQuery(id+"F6.wireOp",EDGE,"E75"),sQuery(id+"F6.wireOp",EDGE,"E76")])],"isStart":false}),makeQuery(id+"F9.opExtrude","CAP_FACE",FACE,{"disambiguationData":[OSD([subQ11,subQ21,subQ8,sQuery(id+"F4.wireOp",EDGE,"E39"),subQ2,sQuery(id+"F4.wireOp",EDGE,"E56"),sQuery(id+"F4.wireOp",EDGE,"E58"),sQuery(id+"F4.wireOp",EDGE,"E59"),sQuery(id+"F4.wireOp",EDGE,"E61")])],"isStart":false}),makeQuery(id+"F9.opExtrude","CAP_FACE",FACE,{"disambiguationData":[OSD([subQ10,subQ21,subQ9,subQ8,subQ2,subQ26,subQ6,subQ0,subQ3,subQ17,subQ5])],"isStart":false}),makeQuery(id+"F10.opExtrude","CAP_FACE",FACE,{"disambiguationData":[OSD([subQ11,subQ10,subQ2,sQuery(id+"F4.wireOp",EDGE,"E43"),subQ26])],"isStart":false})]}),makeQuery(id+"F11.opExtrude","CAP_FACE",FACE,{"disambiguationData":[OSD([subQ11,subQ21,sQuery(id+"F4.wireOp",EDGE,"E54"),sQuery(id+"F4.wireOp",EDGE,"E55")])],"isStart":false})]})})});}
            var Q2;
            Q2=makeQuery(id+"F8.opExtrude","CAP_FACE",FACE,{"disambiguationData":[OSD([sQuery(id+"F2.wireOp",EDGE,"E10"),sQuery(id+"F5.wireOp",EDGE,"E63"),sQuery(id+"F5.wireOp",EDGE,"E65"),sQuery(id+"F5.wireOp",EDGE,"E66"),sQuery(id+"F5.wireOp",EDGE,"E67")])],"isStart":false});
            var Q3;
            Q3=makeQuery(id+"F8.opExtrude","CAP_FACE",FACE,{"disambiguationData":[OSD([sQuery(id+"F2.wireOp",EDGE,"E8"),sQuery(id+"F5.wireOp",EDGE,"E63"),sQuery(id+"F5.wireOp",EDGE,"E64"),sQuery(id+"F5.wireOp",EDGE,"E65")])],"isStart":false});
            extrude(context, id + "F26", {"entities" : qUnion([Q0, Q1, Q2, Q3]), "operationType" : NewBodyOperationType.ADD, "depth" : 1 * mm, "offsetDistance" : 25 * mm});
        }
        {
            var Q0;
            Q0=makeQuery(id+"F13.opExtrude","CAP_FACE",FACE,{"disambiguationData":[OSD([sQuery(id+"F3.wireOp",EDGE,"E22"),sQuery(id+"F3.wireOp",EDGE,"E25"),sQuery(id+"F3.wireOp",EDGE,"E31.MirrorCS"),sQuery(id+"F3.wireOp",EDGE,"E33.MirrorCS")])],"isStart":false});
            var Q1;
            Q1=makeQuery(id+"F13.opExtrude","CAP_FACE",FACE,{"disambiguationData":[OSD([sQuery(id+"F3.wireOp",EDGE,"E23"),sQuery(id+"F3.wireOp",EDGE,"E24"),sQuery(id+"F3.wireOp",EDGE,"E34.MirrorCS"),sQuery(id+"F3.wireOp",EDGE,"E35.MirrorCS")])],"isStart":false});
            var Q2;
            Q2=makeQuery(id+"F13.opExtrude","CAP_FACE",FACE,{"disambiguationData":[OSD([sQuery(id+"F3.wireOp",EDGE,"E26"),sQuery(id+"F3.wireOp",EDGE,"E32.MirrorCS")])],"isStart":false});
            var Q3;
            Q3=makeQuery(id+"F13.opExtrude","CAP_FACE",FACE,{"disambiguationData":[OSD([sQuery(id+"F3.wireOp",EDGE,"E27"),sQuery(id+"F3.wireOp",EDGE,"E28"),sQuery(id+"F3.wireOp",EDGE,"E29.MirrorCS"),sQuery(id+"F3.wireOp",EDGE,"E30.MirrorCS")])],"isStart":false});
            var Q4;
            {var subQ0=sQuery(id+"F2.wireOp",EDGE,"E12");var subQ1=sQuery(id+"F2.wireOp",EDGE,"E9");Q4=makeQuery(id+"F21.boolean.opBoolean","MERGE",FACE,{"derivedFrom":[makeQuery(id+"F14.opExtrude","CAP_FACE",FACE,{"disambiguationData":[OSD([sQuery(id+"F2.wireOp",EDGE,"E8"),subQ1])],"isStart":false}),makeQuery(id+"F19.opExtrude","CAP_FACE",FACE,{"disambiguationData":[OSD([sQuery(id+"F2.wireOp",EDGE,"E10"),sQuery(id+"F2.wireOp",EDGE,"E11"),subQ0])],"isStart":false})],"fromTools":[makeQuery(id+"F21.opExtrude","CAP_FACE",FACE,{"disambiguationData":[OSD([subQ1,subQ0,sQuery(id+"F2.wireOp",EDGE,"E13"),sQuery(id+"F2.wireOp",EDGE,"E15"),sQuery(id+"F2.wireOp",EDGE,"E16")])],"isStart":false})]});}
            extrude(context, id + "F27", {"entities" : qUnion([Q0, Q1, Q2, Q3, Q4]), "operationType" : NewBodyOperationType.ADD, "depth" : 1.24 * mm, "offsetDistance" : 25 * mm});
        }
        {
            var Q0;
            Q0=makeQuery(id+"F12.opExtrude","CAP_FACE",FACE,{"disambiguationData":[OSD([sQuery(id+"F3.wireOp",EDGE,"E22"),sQuery(id+"F3.wireOp",EDGE,"E26"),sQuery(id+"F3.wireOp",EDGE,"E27"),sQuery(id+"F3.wireOp",EDGE,"E29.MirrorCS"),sQuery(id+"F3.wireOp",EDGE,"E31.MirrorCS"),sQuery(id+"F3.wireOp",EDGE,"E32.MirrorCS")])],"isStart":false});
            var Q1;
            {var subQ0=sQuery(id+"F3.wireOp",EDGE,"E26");var subQ1=makeQuery(id+"F13.opExtrude","SWEPT_FACE",FACE,{"disambiguationData":[OSD([subQ0])]});var subQ2=sQuery(id+"F3.wireOp",EDGE,"E34.MirrorCS");var subQ3=sQuery(id+"F3.wireOp",EDGE,"E31.MirrorCS");var subQ4=sQuery(id+"F3.wireOp",EDGE,"E32.MirrorCS");var subQ6=sQuery(id+"F3.wireOp",EDGE,"E23");var subQ7=sQuery(id+"F3.wireOp",EDGE,"E22");Q1=makeQuery(id+"F15.boolean.opBoolean","SPLIT",FACE,{"disambiguationData":[TD([subQ1])],"derivedFrom":makeQuery(id+"F14.boolean.opBoolean","SPLIT",FACE,{"disambiguationData":[TD([subQ1])],"derivedFrom":makeQuery(id+"F12.opExtrude","CAP_FACE",FACE,{"disambiguationData":[OSD([subQ7,subQ6,subQ0,subQ3,subQ4,subQ2])],"isStart":false})})});}
            var Q2;
            {var subQ0=sQuery(id+"F2.wireOp",EDGE,"E13");var subQ1=sQuery(id+"F2.wireOp",EDGE,"E10");var subQ2=sQuery(id+"F2.wireOp",EDGE,"E9");Q2=makeQuery(id+"F23.boolean.opBoolean","MERGE",FACE,{"derivedFrom":[makeQuery(id+"F18.boolean.opBoolean","MERGE",FACE,{"derivedFrom":[makeQuery(id+"F15.opExtrude","CAP_FACE",FACE,{"disambiguationData":[OSD([sQuery(id+"F2.wireOp",EDGE,"E8"),subQ2,subQ1,subQ0,sQuery(id+"F2.wireOp",EDGE,"E21")])],"isStart":false}),makeQuery(id+"F16.opExtrude","CAP_FACE",FACE,{"disambiguationData":[OSD([subQ2,subQ0,sQuery(id+"F2.wireOp",EDGE,"E17"),sQuery(id+"F2.wireOp",EDGE,"E18")])],"isStart":false}),makeQuery(id+"F16.opExtrude","CAP_FACE",FACE,{"disambiguationData":[OSD([subQ1,sQuery(id+"F2.wireOp",EDGE,"E12"),subQ0,sQuery(id+"F2.wireOp",EDGE,"E14")])],"isStart":false}),makeQuery(id+"F18.opExtrude","CAP_FACE",FACE,{"disambiguationData":[OSD([subQ2,subQ1,subQ0,sQuery(id+"F2.wireOp",EDGE,"E19"),sQuery(id+"F2.wireOp",EDGE,"E20")])],"isStart":false})]})],"fromTools":[makeQuery(id+"F23.opExtrude","CAP_FACE",FACE,{"disambiguationData":[OSD([subQ0,sQuery(id+"F2.wireOp",EDGE,"E15"),sQuery(id+"F2.wireOp",EDGE,"E16"),sQuery(id+"F22.wireOp",EDGE,"E77"),sQuery(id+"F22.wireOp",EDGE,"E78"),sQuery(id+"F22.wireOp",EDGE,"E79")])],"isStart":false})]});}
            var Q3;
            Q3=makeQuery(id+"F15.opExtrude","CAP_FACE",FACE,{"disambiguationData":[OSD([sQuery(id+"F2.wireOp",EDGE,"E8"),sQuery(id+"F2.wireOp",EDGE,"E9"),sQuery(id+"F2.wireOp",EDGE,"E11")])],"isStart":false});
            var Q4;
            {var subQ0=sQuery(id+"F3.wireOp",EDGE,"E23");var subQ2=sQuery(id+"F3.wireOp",EDGE,"E22");var subQ3=sQuery(id+"F3.wireOp",EDGE,"E26");var subQ5=sQuery(id+"F3.wireOp",EDGE,"E34.MirrorCS");var subQ6=sQuery(id+"F3.wireOp",EDGE,"E31.MirrorCS");var subQ7=sQuery(id+"F3.wireOp",EDGE,"E32.MirrorCS");Q4=makeQuery(id+"F14.boolean.opBoolean","SPLIT",FACE,{"disambiguationData":[TD([makeQuery(id+"F13.opExtrude","SWEPT_FACE",FACE,{"disambiguationData":[OSD([subQ0])]})])],"derivedFrom":makeQuery(id+"F12.opExtrude","CAP_FACE",FACE,{"disambiguationData":[OSD([subQ2,subQ0,subQ3,subQ6,subQ7,subQ5])],"isStart":false})});}
            var Q5;
            Q5=makeQuery(id+"F12.opExtrude","CAP_FACE",FACE,{"disambiguationData":[OSD([sQuery(id+"F3.wireOp",EDGE,"E22"),sQuery(id+"F3.wireOp",EDGE,"E24"),sQuery(id+"F3.wireOp",EDGE,"E25"),sQuery(id+"F3.wireOp",EDGE,"E31.MirrorCS"),sQuery(id+"F3.wireOp",EDGE,"E33.MirrorCS"),sQuery(id+"F3.wireOp",EDGE,"E35.MirrorCS")])],"isStart":false});
            var Q6;
            Q6=makeQuery(id+"F12.opExtrude","CAP_FACE",FACE,{"disambiguationData":[OSD([sQuery(id+"F3.wireOp",EDGE,"E27"),sQuery(id+"F3.wireOp",EDGE,"E28"),sQuery(id+"F3.wireOp",EDGE,"E29.MirrorCS"),sQuery(id+"F3.wireOp",EDGE,"E30.MirrorCS")])],"isStart":false});
            extrude(context, id + "F28", {"entities" : qUnion([Q0, Q1, Q2, Q3, Q4, Q5, Q6]), "operationType" : NewBodyOperationType.ADD, "depth" : 1 * mm, "offsetDistance" : 25 * mm});
        }
    });
